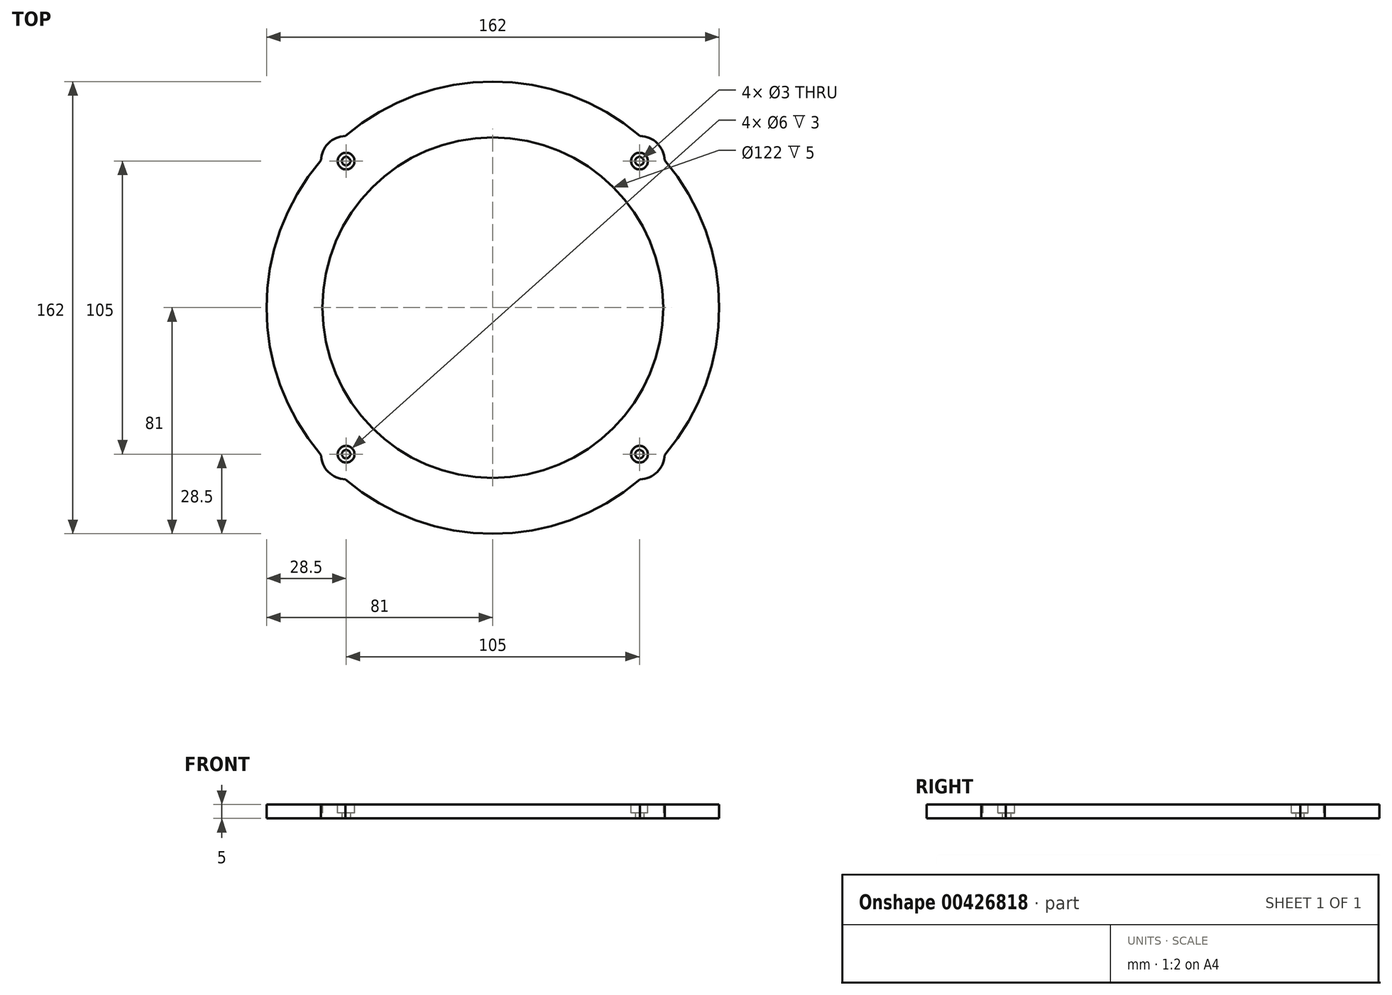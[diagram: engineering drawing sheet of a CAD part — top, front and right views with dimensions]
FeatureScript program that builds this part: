
annotation { "Feature Type Name" : "Feature", "Feature Type Description" : "" }
export const myFeature = defineFeature(function(context is Context, id is Id, definition is map)
    precondition{}
    {
        {
            assignVariable(context, id + "F0", {"name" : "Height", "anyValue" : 5 * mm});
        }
        {
            assignVariable(context, id + "F1", {"name" : "ScrewHeadSinkDepth", "anyValue" : 3 * mm});
        }
        {
            var Q0;
            Q0=qCreatedBy(makeId("Top.planeOp"),FACE);
            var sketch = newSketch(context, id + "F2", { "sketchPlane" : qUnion([Q0])});
            skCircle(sketch, "E0", {"center": v(0, 0) * mm, "radius": 61 * mm});
            skArc(sketch, "E1", {"start": v(-61.5, 52.72) * mm, "mid": v(-81, 0) * mm, "end": v(-61.5, -52.72) * mm});
            skPoint(sketch, "E2", {"position": v(-52.5, 52.5) * mm});
            skArc(sketch, "E3", {"start": v(-52.72, 61.5) * mm, "mid": v(-58.86, 58.86) * mm, "end": v(-61.5, 52.72) * mm});
            skCircle(sketch, "E4", {"center": v(-52.5, 52.5) * mm, "radius": 1.5 * mm});
            skPoint(sketch, "E5.1.0", {"position": v(-52.5, -52.5) * mm});
            skCircle(sketch, "E5.1.1", {"center": v(-52.5, -52.5) * mm, "radius": 1.5 * mm});
            skArc(sketch, "E5.1.2", {"start": v(-61.5, -52.72) * mm, "mid": v(-58.86, -58.86) * mm, "end": v(-52.72, -61.5) * mm});
            skPoint(sketch, "E5.2.0", {"position": v(52.5, -52.5) * mm});
            skCircle(sketch, "E5.2.1", {"center": v(52.5, -52.5) * mm, "radius": 1.5 * mm});
            skArc(sketch, "E5.2.2", {"start": v(52.72, -61.5) * mm, "mid": v(58.86, -58.86) * mm, "end": v(61.5, -52.72) * mm});
            skPoint(sketch, "E5.3.0", {"position": v(52.5, 52.5) * mm});
            skCircle(sketch, "E5.3.1", {"center": v(52.5, 52.5) * mm, "radius": 1.5 * mm});
            skArc(sketch, "E5.3.2", {"start": v(61.5, 52.72) * mm, "mid": v(58.86, 58.86) * mm, "end": v(52.72, 61.5) * mm});
            skArc(sketch, "E6.trimOffspring", {"start": v(52.72, 61.5) * mm, "mid": v(0, 81) * mm, "end": v(-52.72, 61.5) * mm});
            skArc(sketch, "E7.trimOffspring", {"start": v(61.5, -52.72) * mm, "mid": v(81, 0) * mm, "end": v(61.5, 52.72) * mm});
            skArc(sketch, "E8.trimOffspring", {"start": v(-52.72, -61.5) * mm, "mid": v(0, -81) * mm, "end": v(52.72, -61.5) * mm});
            skCircle(sketch, "E9", {"center": v(0, 0) * mm, "radius": 56 * mm, "construction": true});
            skSolve(sketch);
        }
        {
            var Q0;
            Q0=makeQuery(id+"F2.imprint","IMPRINT",FACE,{"disambiguationData":[TD([[makeQuery(id+"F2.imprint","IMPRINT",EDGE,{"derivedFrom":sQuery(id+"F2.wireOp",EDGE,"E0")}),-1.0]])]});
            extrude(context, id + "F3", {"entities" : qUnion([Q0]), "depth" : getVariable(context, 'Height')});
        }
        {
            var Q0;
            Q0=makeQuery(id+"F3.opExtrude","CAP_FACE",FACE,{"disambiguationData":[OSD([sQuery(id+"F2.wireOp",EDGE,"E0"),sQuery(id+"F2.wireOp",EDGE,"E1"),sQuery(id+"F2.wireOp",EDGE,"E3"),sQuery(id+"F2.wireOp",EDGE,"E4"),sQuery(id+"F2.wireOp",EDGE,"E5.1.1"),sQuery(id+"F2.wireOp",EDGE,"E5.1.2"),sQuery(id+"F2.wireOp",EDGE,"E5.2.1"),sQuery(id+"F2.wireOp",EDGE,"E5.2.2"),sQuery(id+"F2.wireOp",EDGE,"E5.3.1"),sQuery(id+"F2.wireOp",EDGE,"E5.3.2"),sQuery(id+"F2.wireOp",EDGE,"E6.trimOffspring"),sQuery(id+"F2.wireOp",EDGE,"E7.trimOffspring"),sQuery(id+"F2.wireOp",EDGE,"E8.trimOffspring")])],"isStart":false});
            var sketch = newSketch(context, id + "F4", { "sketchPlane" : qUnion([Q0])});
            skCircle(sketch, "E10", {"center": v(-52.5, 52.5) * mm, "radius": 3 * mm});
            skCircle(sketch, "E11.1.0", {"center": v(-52.5, -52.5) * mm, "radius": 3 * mm});
            skCircle(sketch, "E11.2.0", {"center": v(52.5, -52.5) * mm, "radius": 3 * mm});
            skCircle(sketch, "E11.3.0", {"center": v(52.5, 52.5) * mm, "radius": 3 * mm});
            skPoint(sketch, "E11.center", {"position": v(0, 0) * mm});
            skSolve(sketch);
        }
        {
            var Q0;
            Q0=makeQuery(id+"F4.imprint","IMPRINT",FACE,{"disambiguationData":[TD([[makeQuery(id+"F4.imprint","IMPRINT",EDGE,{"derivedFrom":sQuery(id+"F4.wireOp",EDGE,"E10")}),1.0]])]});
            var Q1;
            Q1=makeQuery(id+"F4.imprint","IMPRINT",FACE,{"disambiguationData":[TD([[makeQuery(id+"F4.imprint","IMPRINT",EDGE,{"derivedFrom":sQuery(id+"F4.wireOp",EDGE,"E11.3.0")}),1.0]])]});
            var Q2;
            Q2=makeQuery(id+"F4.imprint","IMPRINT",FACE,{"disambiguationData":[TD([[makeQuery(id+"F4.imprint","IMPRINT",EDGE,{"derivedFrom":sQuery(id+"F4.wireOp",EDGE,"E11.1.0")}),1.0]])]});
            var Q3;
            Q3=makeQuery(id+"F4.imprint","IMPRINT",FACE,{"disambiguationData":[TD([[makeQuery(id+"F4.imprint","IMPRINT",EDGE,{"derivedFrom":sQuery(id+"F4.wireOp",EDGE,"E11.2.0")}),1.0]])]});
            var Q4;
            Q4=sQuery(id+"F4.wireOp",EDGE,"E10");
            var Q5;
            Q5=sQuery(id+"F4.wireOp",EDGE,"E11.1.0");
            var Q6;
            Q6=sQuery(id+"F4.wireOp",EDGE,"E11.2.0");
            var Q7;
            Q7=sQuery(id+"F4.wireOp",EDGE,"E11.3.0");
            extrude(context, id + "F5", {"entities" : qUnion([Q0, Q1, Q2, Q3]), "operationType" : NewBodyOperationType.REMOVE, "surfaceEntities" : qUnion([Q4, Q5, Q6, Q7]), "oppositeDirection" : true, "depth" : getVariable(context, 'ScrewHeadSinkDepth')});
        }
    });
